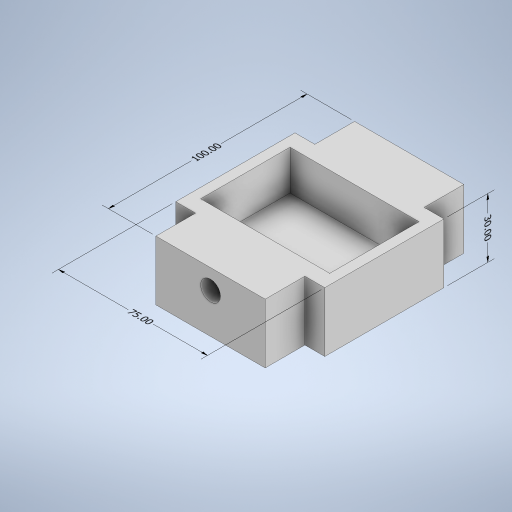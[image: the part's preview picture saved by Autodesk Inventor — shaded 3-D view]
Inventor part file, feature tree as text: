
AUTODESK INVENTOR PART (.ipt)
format: ipt  version: 2023 (Build 270158000, 158)  size: 275,968 bytes
history: native  units: mm
features: other x5, extrude x4, sketch x4
ambient origin geometry x8: Origin, YZ Plane, XZ Plane, XY Plane, X Axis, Y Axis, Z Axis, Center Point
bodies: Body1 (feature_tree)
feature tree (13):
  other  "Sólido1"
  other  "Anotaciones"
  extrude  "Extrusión1"  Depth=100.0mm
  extrude  "Extrusión3"  Depth=10.0mm
  extrude  "Extrusión7"  Depth=15.0mm TaperAngle=0.0deg
  extrude  "Extrusión8"  Depth=60.0mm
  sketch  "Boceto1"  dims[d0=55.0mm d1=100.0mm]
  sketch  "Boceto3"  dims[d2=30.0mm d3=0.0mm d10=10.0mm]
  sketch  "Boceto9"  dims[d11=10.0mm d12=15.0mm d13=0.0mm]
  sketch  "Boceto10"  dims[d52=75.0mm d53=60.0mm d54=30.0mm d55=0.0mm d56=65.0mm d57=45.0mm d58=20.0mm d59=0.0mm d49=6.905403mm d50=1.213278mm d51=100.0mm d60=4.54591mm d61=7.981576mm d62=75.0mm d63=2.698136mm d64=6.842732mm d65=30.0mm]
  other  "Cota lineal 3"
  other  "Cota lineal 4"
  other  "Cota lineal 5"
